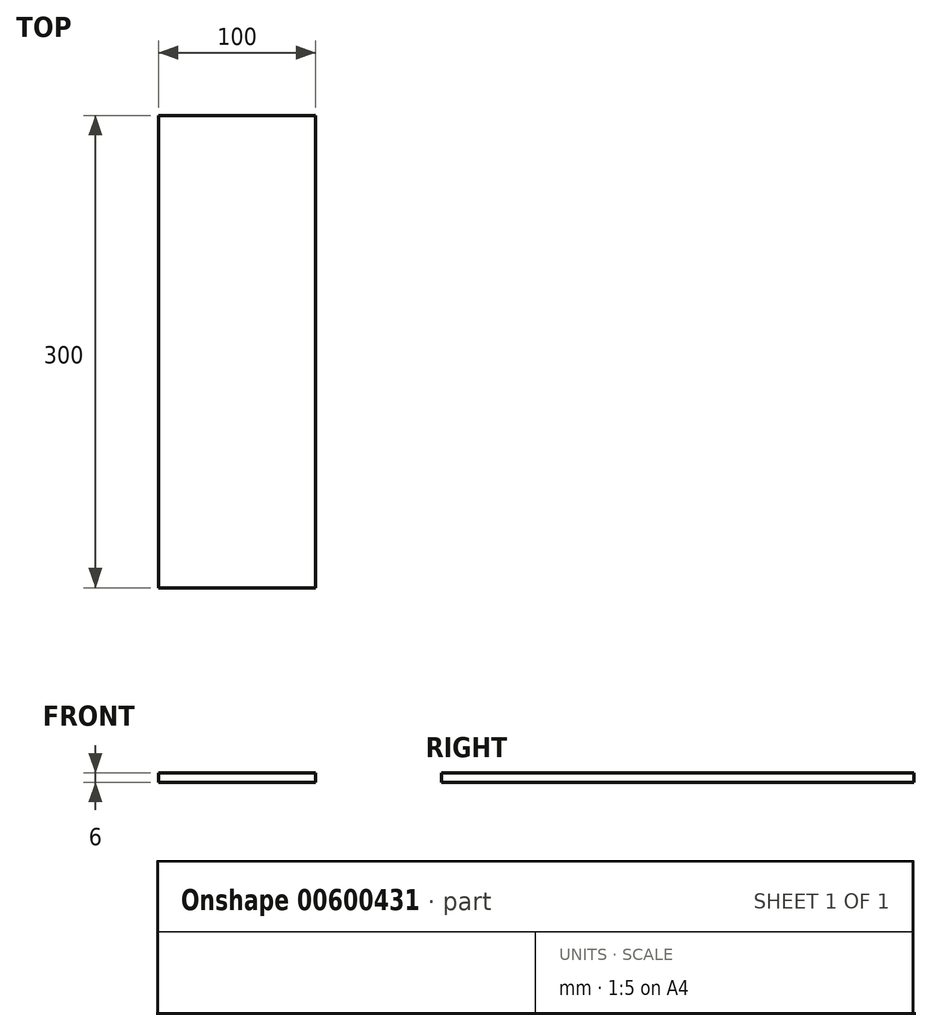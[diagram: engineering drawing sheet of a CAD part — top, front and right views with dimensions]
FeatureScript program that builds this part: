
annotation { "Feature Type Name" : "Feature", "Feature Type Description" : "" }
export const myFeature = defineFeature(function(context is Context, id is Id, definition is map)
    precondition{}
    {
        {
            var Q0;
            Q0=qCreatedBy(makeId("Top.planeOp"),FACE);
            var sketch = newSketch(context, id + "F0", { "sketchPlane" : qUnion([Q0])});
            skLineSegment(sketch, "E0.bottom", {"start": v(-418.57, 104.93) * mm, "end": v(-318.57, 104.93) * mm});
            skLineSegment(sketch, "E0.top", {"start": v(-418.57, -195.07) * mm, "end": v(-318.57, -195.07) * mm});
            skLineSegment(sketch, "E0.left", {"start": v(-418.57, 104.93) * mm, "end": v(-418.57, -195.07) * mm});
            skLineSegment(sketch, "E0.right", {"start": v(-318.57, 104.93) * mm, "end": v(-318.57, -195.07) * mm});
            skSolve(sketch);
        }
        {
            var Q0;
            Q0 = qSketchRegion(id + "F0", true);
            extrude(context, id + "F1", {"entities" : qUnion([Q0]), "depth" : 6 * mm, "offsetDistance" : 25 * mm});
        }
    });
